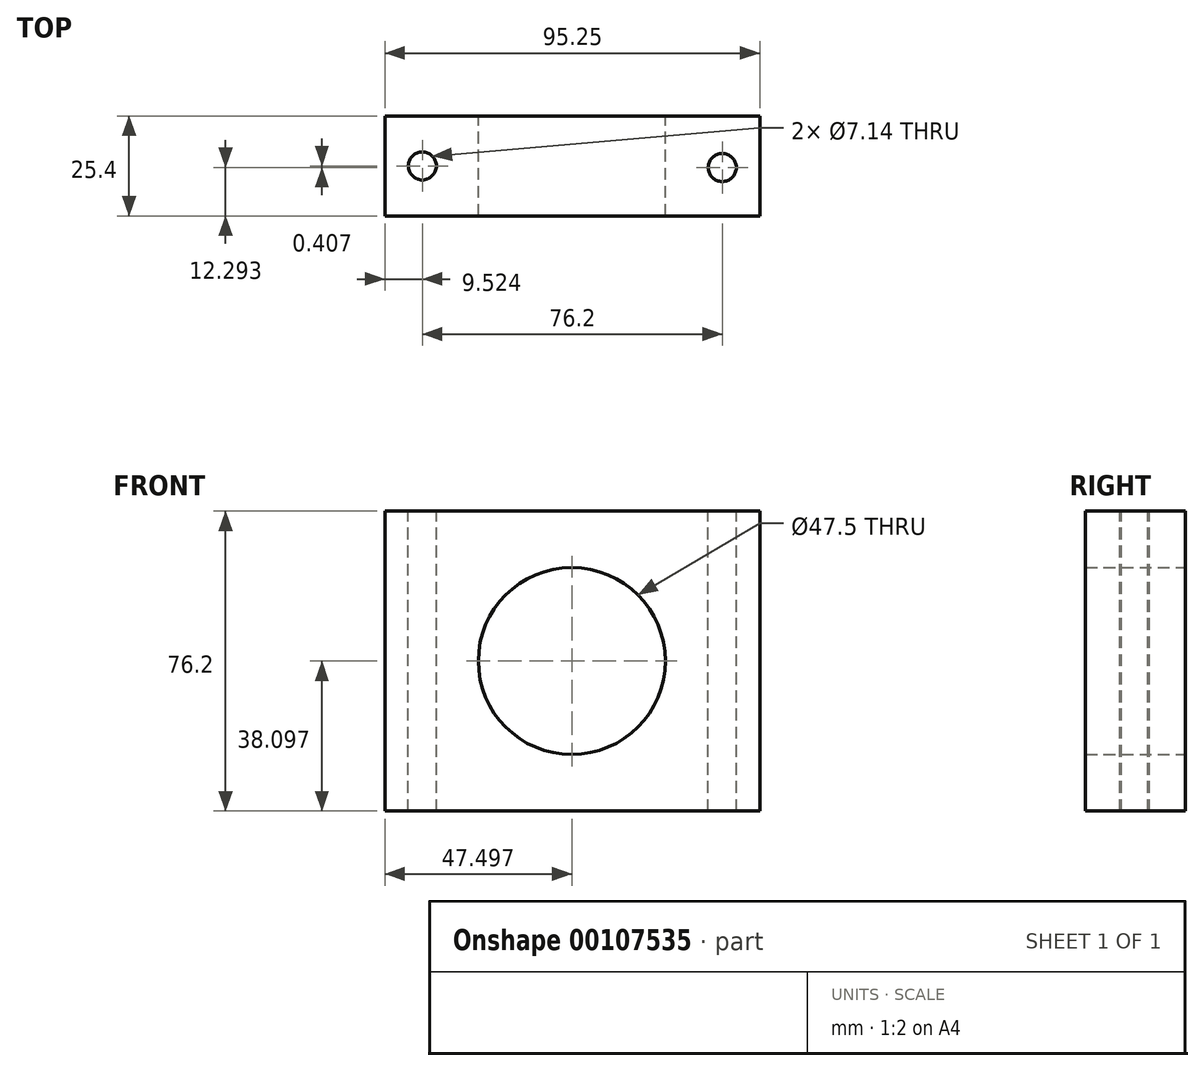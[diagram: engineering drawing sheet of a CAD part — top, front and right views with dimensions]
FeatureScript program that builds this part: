
annotation { "Feature Type Name" : "Feature", "Feature Type Description" : "" }
export const myFeature = defineFeature(function(context is Context, id is Id, definition is map)
    precondition{}
    {
        {
            var Q0;
            Q0=qCreatedBy(makeId("Front.planeOp"),FACE);
            var sketch = newSketch(context, id + "F0", { "sketchPlane" : qUnion([Q0])});
            skLineSegment(sketch, "E0", {"start": v(-57.93, 44.9) * mm, "end": v(-57.93, -31.3) * mm});
            skLineSegment(sketch, "E1", {"start": v(-57.93, -31.3) * mm, "end": v(37.32, -31.3) * mm});
            skLineSegment(sketch, "E2", {"start": v(-57.93, 44.9) * mm, "end": v(37.32, 44.9) * mm});
            skLineSegment(sketch, "E3", {"start": v(37.32, 44.9) * mm, "end": v(37.32, -31.3) * mm});
            skCircle(sketch, "E4", {"center": v(-10.43, 6.8) * mm, "radius": 23.75 * mm});
            skSolve(sketch);
        }
        {
            var Q0;
            Q0=makeQuery(id+"F0.imprint","IMPRINT",FACE,{"disambiguationData":[TD([[makeQuery(id+"F0.imprint","IMPRINT",EDGE,{"derivedFrom":sQuery(id+"F0.wireOp",EDGE,"E0")}),1.0]])]});
            extrude(context, id + "F1", {"entities" : qUnion([Q0]), "depth" : 25.4 * mm});
        }
        {
            var Q0;
            Q0=makeQuery(id+"F1.opExtrude","SWEPT_FACE",FACE,{"disambiguationData":[OSD([sQuery(id+"F0.wireOp",EDGE,"E2")])]});
            var sketch = newSketch(context, id + "F2", { "sketchPlane" : qUnion([Q0])});
            skCircle(sketch, "E5", {"center": v(-48.4, -12.7) * mm, "radius": 3.57 * mm});
            skCircle(sketch, "E6", {"center": v(27.8, -13.1) * mm, "radius": 3.57 * mm});
            skSolve(sketch);
        }
        {
            var Q0;
            Q0=makeQuery(id+"F2.imprint","IMPRINT",FACE,{"disambiguationData":[TD([[makeQuery(id+"F2.imprint","IMPRINT",EDGE,{"derivedFrom":sQuery(id+"F2.wireOp",EDGE,"E5")}),1.0]])]});
            var Q1;
            Q1=makeQuery(id+"F2.imprint","IMPRINT",FACE,{"disambiguationData":[TD([[makeQuery(id+"F2.imprint","IMPRINT",EDGE,{"derivedFrom":sQuery(id+"F2.wireOp",EDGE,"E6")}),1.0]])]});
            extrude(context, id + "F3", {"entities" : qUnion([Q0, Q1]), "operationType" : NewBodyOperationType.REMOVE, "endBound" : BoundingType.THROUGH_ALL, "oppositeDirection" : true, "depth" : 25.4 * mm});
        }
    });
